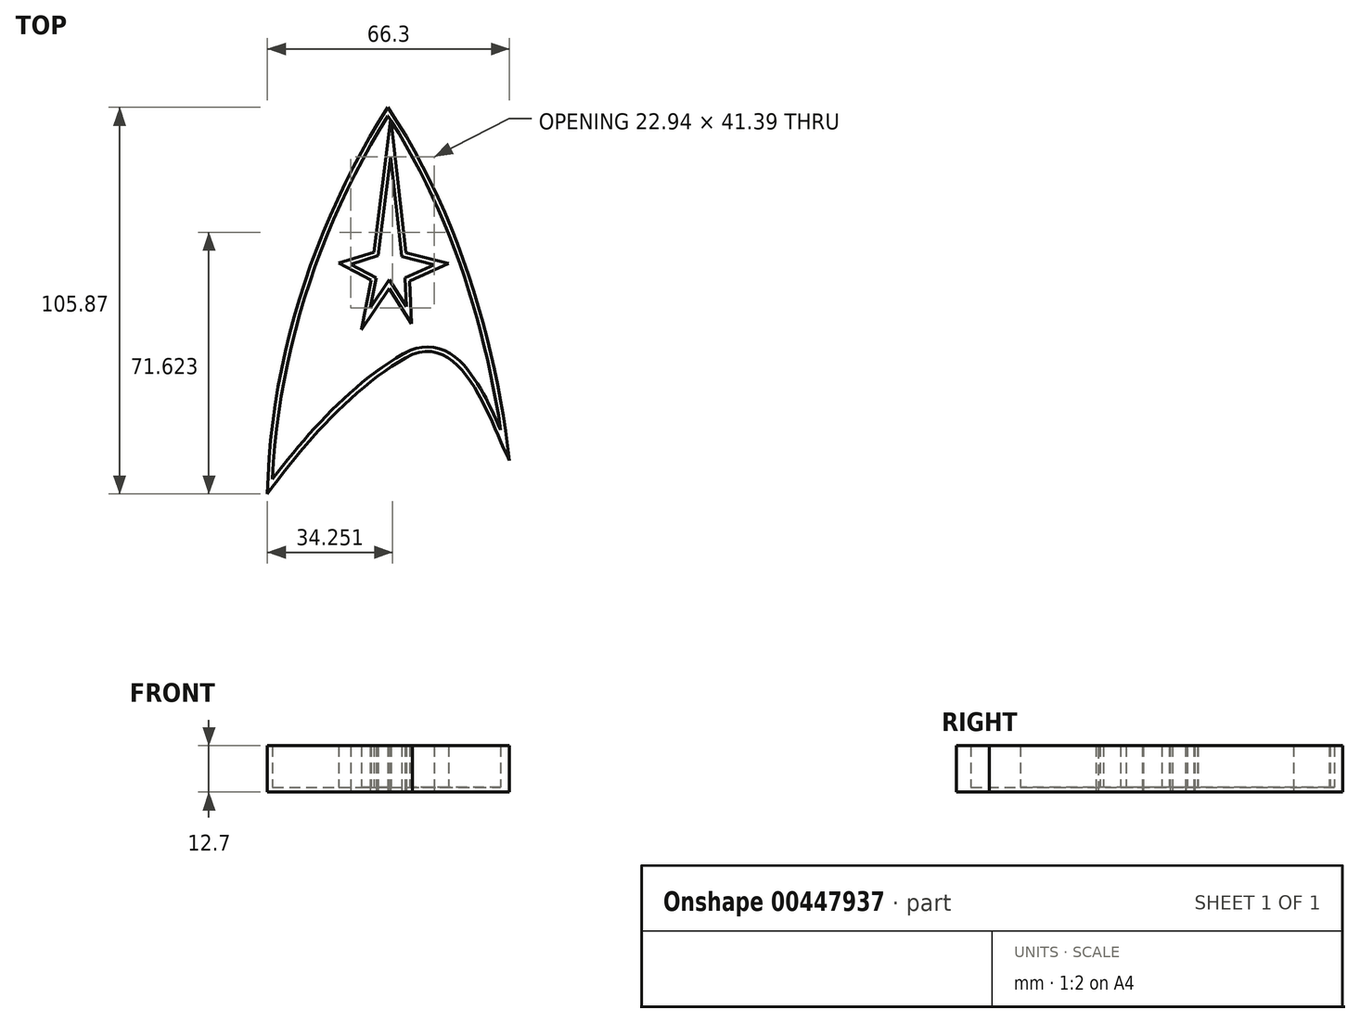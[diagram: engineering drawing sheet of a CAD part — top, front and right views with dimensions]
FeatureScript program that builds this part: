
annotation { "Feature Type Name" : "Feature", "Feature Type Description" : "" }
export const myFeature = defineFeature(function(context is Context, id is Id, definition is map)
    precondition{}
    {
        {
            var Q0;
            Q0=qCreatedBy(makeId("Top.planeOp"),FACE);
            var sketch = newSketch(context, id + "F0", { "sketchPlane" : qUnion([Q0])});
            skPoint(sketch, "E0.1.internal.snap0", {"position": v(-6.72, 62.98) * mm});
            skFitSpline(sketch, "E0", {"points": [v(-39.7, -47.3) * mm, v(-6.72, 58.58) * mm], "startDerivative": vector(2.03, 112.64) * mm, "endDerivative": vector(58.35, 91.33) * mm});
            skFitSpline(sketch, "E1", {"points": [v(-6.72, 58.58) * mm, v(26.6, -38.16) * mm], "startDerivative": vector(60.38, -90.32) * mm, "endDerivative": vector(11.16, -92.35) * mm});
            skFitSpline(sketch, "E2", {"points": [v(26.6, -38.16) * mm, v(0, -9.07) * mm], "startDerivative": vector(-17.25, 34.5) * mm, "endDerivative": vector(-42.23, -16.24) * mm});
            skFitSpline(sketch, "E3", {"points": [v(-39.7, -47.3) * mm, v(0, -9.07) * mm], "startDerivative": vector(31.46, 43.64) * mm, "endDerivative": vector(44.02, 22.33) * mm});
            skLineSegment(sketch, "E4", {"start": v(-6, 45.03) * mm, "end": v(-9.4, 17.97) * mm});
            skLineSegment(sketch, "E5", {"start": v(-16.93, 15.64) * mm, "end": v(-9.4, 17.97) * mm});
            skLineSegment(sketch, "E6", {"start": v(-16.93, 15.64) * mm, "end": v(-9.94, 11.88) * mm});
            skLineSegment(sketch, "E7", {"start": v(-9.94, 11.88) * mm, "end": v(-11.55, 3.64) * mm});
            skLineSegment(sketch, "E8", {"start": v(-11.55, 3.64) * mm, "end": v(-6.35, 11.34) * mm});
            skLineSegment(sketch, "E9", {"start": v(-6.35, 11.34) * mm, "end": v(-1.7, 4) * mm});
            skLineSegment(sketch, "E10", {"start": v(-6, 45.03) * mm, "end": v(-2.95, 17.8) * mm});
            skLineSegment(sketch, "E11", {"start": v(-2.95, 17.8) * mm, "end": v(6, 15.46) * mm});
            skLineSegment(sketch, "E12", {"start": v(6, 15.46) * mm, "end": v(-2.05, 11.88) * mm});
            skLineSegment(sketch, "E13", {"start": v(-2.05, 11.88) * mm, "end": v(-1.7, 4) * mm});
            skSolve(sketch);
        }
        {
            var Q0;
            Q0=makeQuery(id+"F0.imprint","IMPRINT",FACE,{"disambiguationData":[TD([[makeQuery(id+"F0.imprint","IMPRINT",EDGE,{"derivedFrom":sQuery(id+"F0.wireOp",EDGE,"E0")}),-1.0]])]});
            extrude(context, id + "F1", {"entities" : qUnion([Q0]), "depth" : 12.7 * mm});
        }
        {
            var Q0;
            Q0=makeQuery(id+"F1.opExtrude","CAP_FACE",FACE,{"disambiguationData":[OSD([sQuery(id+"F0.wireOp",EDGE,"E0"),sQuery(id+"F0.wireOp",EDGE,"E1"),sQuery(id+"F0.wireOp",EDGE,"E2"),sQuery(id+"F0.wireOp",EDGE,"E3"),sQuery(id+"F0.wireOp",EDGE,"E4"),sQuery(id+"F0.wireOp",EDGE,"E5"),sQuery(id+"F0.wireOp",EDGE,"E6"),sQuery(id+"F0.wireOp",EDGE,"E7"),sQuery(id+"F0.wireOp",EDGE,"E8"),sQuery(id+"F0.wireOp",EDGE,"E9"),sQuery(id+"F0.wireOp",EDGE,"E10"),sQuery(id+"F0.wireOp",EDGE,"E11"),sQuery(id+"F0.wireOp",EDGE,"E12"),sQuery(id+"F0.wireOp",EDGE,"E13")])],"isStart":false});
            shell(context, id + "F2", {"entities" : qUnion([Q0]), "thickness" : 1.27 * mm});
        }
    });
